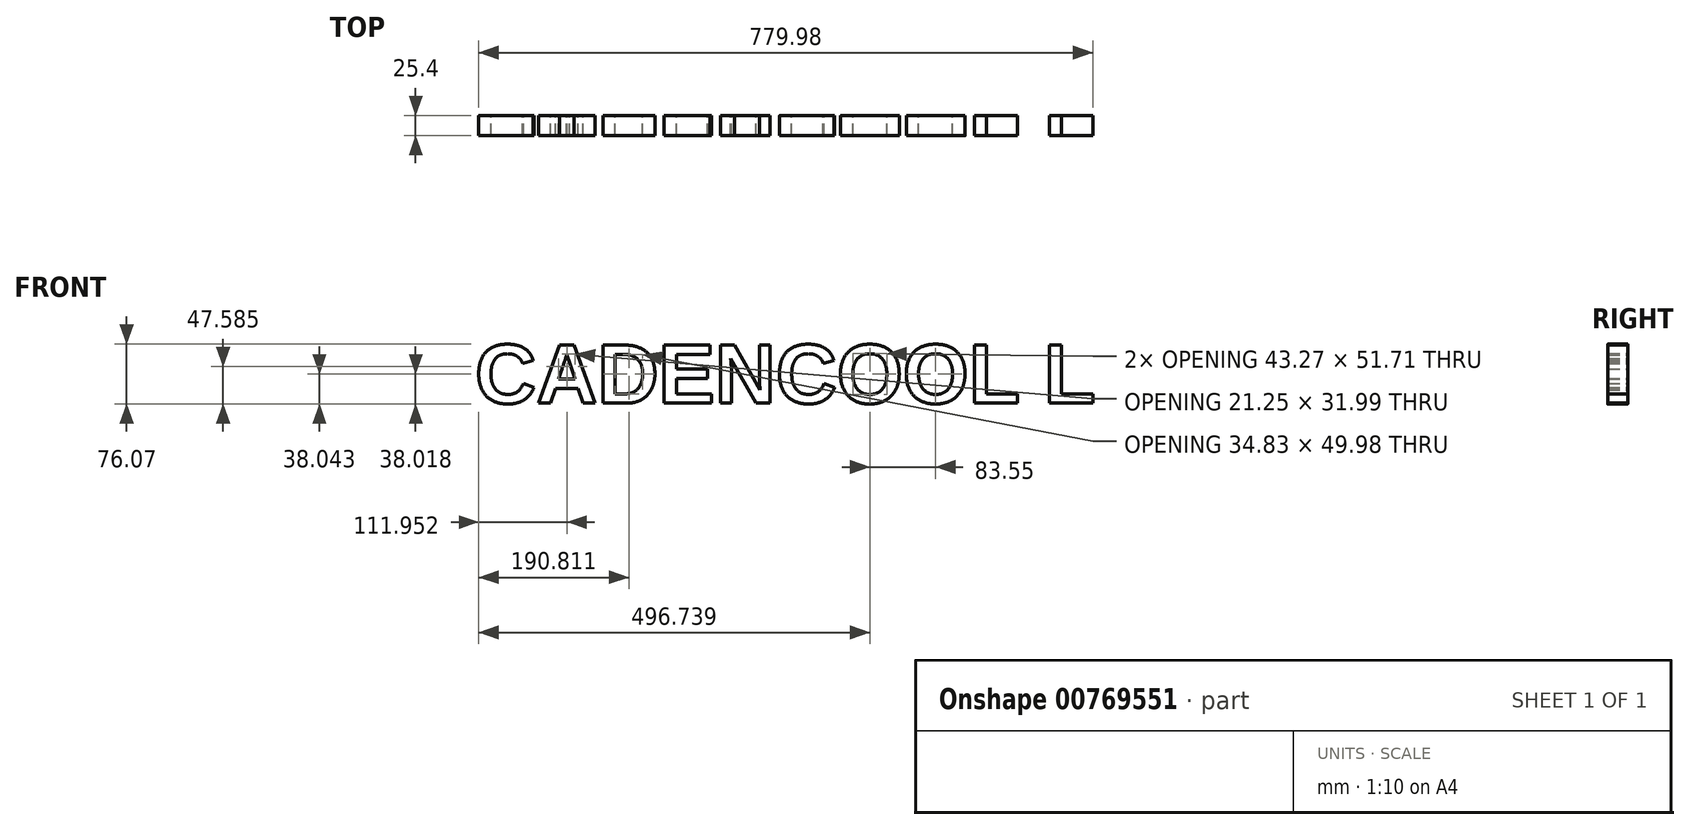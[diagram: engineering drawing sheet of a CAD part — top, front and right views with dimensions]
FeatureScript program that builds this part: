
annotation { "Feature Type Name" : "Feature", "Feature Type Description" : "" }
export const myFeature = defineFeature(function(context is Context, id is Id, definition is map)
    precondition{}
    {
        {
            var Q0;
            Q0=qCreatedBy(makeId("Front.planeOp"),FACE);
            var sketch = newSketch(context, id + "F0", { "sketchPlane" : qUnion([Q0])});
            skText(sketch, "E0", { "text": "CADENCOOL L", "fontName": "Arimo-Bold.ttf"});
            const initialGuessF0  = {"E0": [-0.13593, -0.04707, 1, 0, 0.07734]};
            skSetInitialGuess(sketch, initialGuessF0);
            skSolve(sketch);
        }
        {
            var Q0;
            Q0 = qSketchRegion(id + "F0", true);
            extrude(context, id + "F1", {"entities" : qUnion([Q0]), "depth" : 25.4 * mm, "offsetDistance" : 25.4 * mm});
        }
    });
